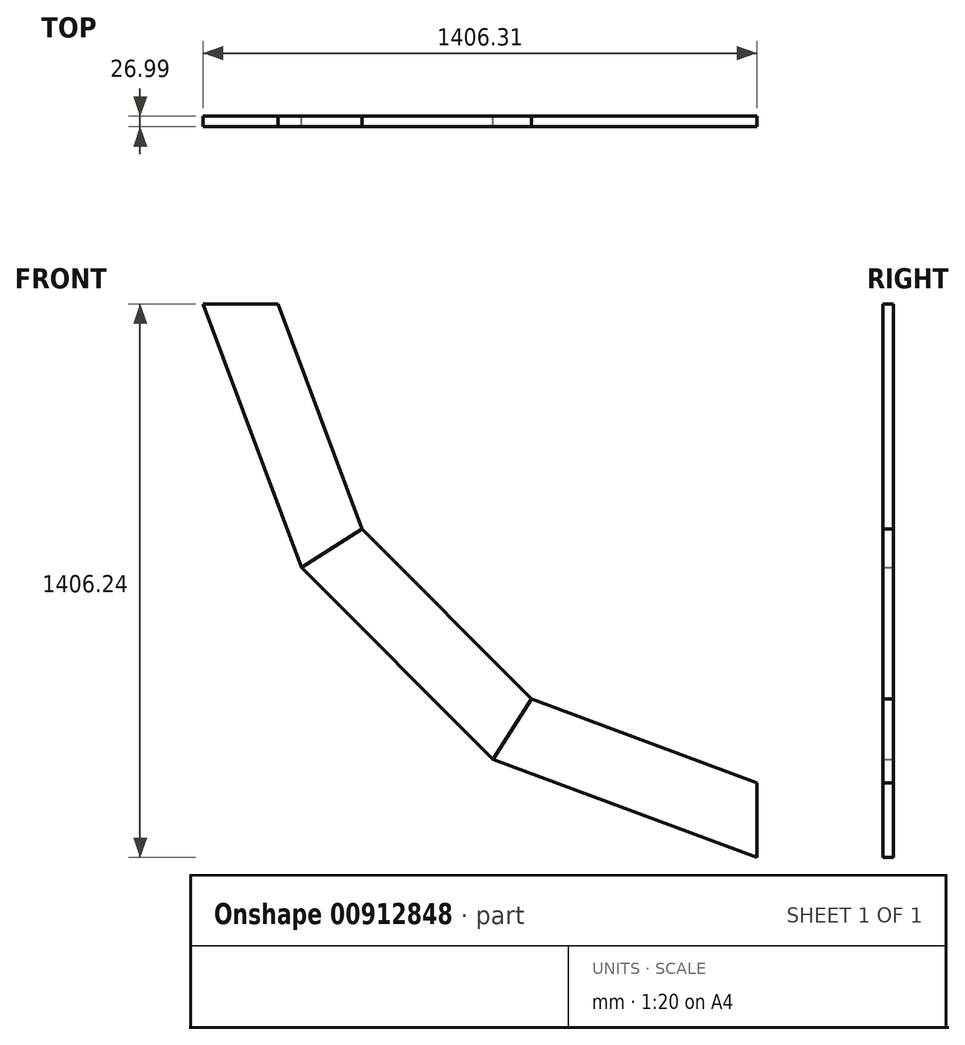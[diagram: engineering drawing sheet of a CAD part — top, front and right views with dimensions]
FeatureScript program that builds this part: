
annotation { "Feature Type Name" : "Feature", "Feature Type Description" : "" }
export const myFeature = defineFeature(function(context is Context, id is Id, definition is map)
    precondition{}
    {
        {
            var Q0;
            Q0=qCreatedBy(makeId("Front.planeOp"),FACE);
            var sketch = newSketch(context, id + "F0", { "sketchPlane" : qUnion([Q0])});
            skLineSegment(sketch, "E0", {"start": v(2153.22, 0) * mm, "end": v(0, 0) * mm, "construction": true});
            skLineSegment(sketch, "E1", {"start": v(0, 0) * mm, "end": v(0, 1924.25) * mm, "construction": true});
            skArc(sketch, "E2", {"start": v(0, 1275.2) * mm, "mid": v(409.72, 409.72) * mm, "end": v(1275.2, 0) * mm});
            skLineSegment(sketch, "E3", {"start": v(0, 1275.2) * mm, "end": v(1275.2, 0) * mm, "construction": true});
            skArc(sketch, "E4.0", {"start": v(51.06, 1275.2) * mm, "mid": v(445.65, 445.65) * mm, "end": v(1275.2, 51.06) * mm});
            skArc(sketch, "E5.0", {"start": v(-63.8, 1275.2) * mm, "mid": v(364.82, 364.82) * mm, "end": v(1275.2, -63.8) * mm});
            skLineSegment(sketch, "E6", {"start": v(-728.5, 1275.2) * mm, "end": v(574.74, 1275.2) * mm, "construction": true});
            skLineSegment(sketch, "E7", {"start": v(1275.2, -744.23) * mm, "end": v(1275.2, 559) * mm, "construction": true});
            skLineSegment(sketch, "E8", {"start": v(51.06, 1275.2) * mm, "end": v(51.06, 1921.78) * mm});
            skLineSegment(sketch, "E9", {"start": v(-63.8, 1275.2) * mm, "end": v(-63.8, 1924.25) * mm});
            skLineSegment(sketch, "E10", {"start": v(1275.2, 51.06) * mm, "end": v(1997.7, 51.06) * mm});
            skLineSegment(sketch, "E11", {"start": v(1275.2, -63.8) * mm, "end": v(2006.98, -63.8) * mm});
            skLineSegment(sketch, "E12", {"start": v(-728.5, 1275.2) * mm, "end": v(1275.2, -744.23) * mm, "construction": true});
            skLineSegment(sketch, "E13", {"start": v(-131.11, 1275.2) * mm, "end": v(119.08, 605.18) * mm});
            skLineSegment(sketch, "E14", {"start": v(58.68, 1275.2) * mm, "end": v(272.16, 703.49) * mm});
            skLineSegment(sketch, "E15", {"start": v(1275.2, 58.68) * mm, "end": v(703.26, 271.54) * mm});
            skLineSegment(sketch, "E16", {"start": v(1275.2, -131.04) * mm, "end": v(604.84, 118.45) * mm});
            skLineSegment(sketch, "E17", {"start": v(272.16, 703.49) * mm, "end": v(703.26, 271.54) * mm});
            skLineSegment(sketch, "E18", {"start": v(119.08, 605.18) * mm, "end": v(604.84, 118.45) * mm});
            skPoint(sketch, "E19", {"position": v(1275.2, -92.61) * mm});
            skLineSegment(sketch, "E20", {"start": v(703.26, 271.54) * mm, "end": v(604.84, 118.45) * mm});
            skLineSegment(sketch, "E21", {"start": v(1275.2, 58.68) * mm, "end": v(1275.2, -131.04) * mm});
            skLineSegment(sketch, "E22", {"start": v(272.16, 703.49) * mm, "end": v(119.08, 605.18) * mm});
            skLineSegment(sketch, "E23", {"start": v(58.68, 1275.2) * mm, "end": v(-131.11, 1275.2) * mm});
            skPoint(sketch, "E24", {"position": v(-76.88, 1275.2) * mm});
            skLineSegment(sketch, "E25", {"start": v(-36.22, 1275.2) * mm, "end": v(195.62, 654.33) * mm, "construction": true});
            skLineSegment(sketch, "E26", {"start": v(195.62, 654.33) * mm, "end": v(654.05, 195) * mm, "construction": true});
            skLineSegment(sketch, "E27", {"start": v(654.05, 195) * mm, "end": v(1275.2, -36.18) * mm, "construction": true});
            skSolve(sketch);
        }
        {
            var Q0;
            {var subQ5=sQuery(id+"F0.wireOp",EDGE,"E14");Q0=makeQuery(id+"F0.imprint","IMPRINT",FACE,{"disambiguationData":[TD([[makeQuery(id+"F0.imprint","IMPRINT",EDGE,{"derivedFrom":subQ5}),-1.0]])]});}
            var Q1;
            {var subQ0=sQuery(id+"F0.wireOp",EDGE,"E23");var subQ1=sQuery(id+"F0.wireOp",EDGE,"E2");var subQ2=makeQuery(id+"F0.imprint","INTERSECT",VERTEX,{"derivedFrom":[subQ1,subQ0]});Q1=makeQuery(id+"F0.imprint","IMPRINT",FACE,{"disambiguationData":[TD([[makeQuery(id+"F0.imprint","IMPRINT",EDGE,{"disambiguationData":[TD([[subQ2,-1.0]])],"derivedFrom":subQ1}),1.0]])]});}
            var Q2;
            {var subQ0=sQuery(id+"F0.wireOp",EDGE,"E23");var subQ1=sQuery(id+"F0.wireOp",EDGE,"E2");var subQ2=makeQuery(id+"F0.imprint","INTERSECT",VERTEX,{"derivedFrom":[subQ1,subQ0]});Q2=makeQuery(id+"F0.imprint","IMPRINT",FACE,{"disambiguationData":[TD([[makeQuery(id+"F0.imprint","IMPRINT",EDGE,{"disambiguationData":[TD([[subQ2,-1.0]])],"derivedFrom":subQ1}),-1.0]])]});}
            var Q3;
            {var subQ5=sQuery(id+"F0.wireOp",EDGE,"E13");Q3=makeQuery(id+"F0.imprint","IMPRINT",FACE,{"disambiguationData":[TD([[makeQuery(id+"F0.imprint","IMPRINT",EDGE,{"derivedFrom":subQ5}),1.0]])]});}
            var Q4;
            {var subQ5=sQuery(id+"F0.wireOp",EDGE,"E15");Q4=makeQuery(id+"F0.imprint","IMPRINT",FACE,{"disambiguationData":[TD([[makeQuery(id+"F0.imprint","IMPRINT",EDGE,{"derivedFrom":subQ5}),1.0]])]});}
            var Q5;
            {var subQ0=sQuery(id+"F0.wireOp",EDGE,"E21");var subQ1=sQuery(id+"F0.wireOp",EDGE,"E2");var subQ2=makeQuery(id+"F0.imprint","INTERSECT",VERTEX,{"derivedFrom":[subQ1,subQ0]});Q5=makeQuery(id+"F0.imprint","IMPRINT",FACE,{"disambiguationData":[TD([[makeQuery(id+"F0.imprint","IMPRINT",EDGE,{"disambiguationData":[TD([[subQ2,1.0]])],"derivedFrom":subQ1}),1.0]])]});}
            var Q6;
            {var subQ0=sQuery(id+"F0.wireOp",EDGE,"E21");var subQ1=sQuery(id+"F0.wireOp",EDGE,"E2");var subQ2=makeQuery(id+"F0.imprint","INTERSECT",VERTEX,{"derivedFrom":[subQ1,subQ0]});Q6=makeQuery(id+"F0.imprint","IMPRINT",FACE,{"disambiguationData":[TD([[makeQuery(id+"F0.imprint","IMPRINT",EDGE,{"disambiguationData":[TD([[subQ2,1.0]])],"derivedFrom":subQ1}),-1.0]])]});}
            var Q7;
            {var subQ5=sQuery(id+"F0.wireOp",EDGE,"E16");Q7=makeQuery(id+"F0.imprint","IMPRINT",FACE,{"disambiguationData":[TD([[makeQuery(id+"F0.imprint","IMPRINT",EDGE,{"derivedFrom":subQ5}),-1.0]])]});}
            extrude(context, id + "F1", {"entities" : qUnion([Q0, Q1, Q2, Q3, Q4, Q5, Q6, Q7]), "depth" : 26.99 * mm, "offsetDistance" : 25.4 * mm});
        }
        {
            var Q0;
            {var subQ5=sQuery(id+"F0.wireOp",EDGE,"E17");Q0=makeQuery(id+"F0.imprint","IMPRINT",FACE,{"disambiguationData":[TD([[makeQuery(id+"F0.imprint","IMPRINT",EDGE,{"derivedFrom":subQ5}),-1.0]])]});}
            var Q1;
            {var subQ0=sQuery(id+"F0.wireOp",EDGE,"E22");var subQ1=sQuery(id+"F0.wireOp",EDGE,"E2");var subQ2=makeQuery(id+"F0.imprint","INTERSECT",VERTEX,{"derivedFrom":[subQ1,subQ0]});Q1=makeQuery(id+"F0.imprint","IMPRINT",FACE,{"disambiguationData":[TD([[makeQuery(id+"F0.imprint","IMPRINT",EDGE,{"disambiguationData":[TD([[subQ2,-1.0]])],"derivedFrom":subQ1}),1.0]])]});}
            var Q2;
            {var subQ0=sQuery(id+"F0.wireOp",EDGE,"E22");var subQ1=sQuery(id+"F0.wireOp",EDGE,"E2");var subQ2=makeQuery(id+"F0.imprint","INTERSECT",VERTEX,{"derivedFrom":[subQ1,subQ0]});Q2=makeQuery(id+"F0.imprint","IMPRINT",FACE,{"disambiguationData":[TD([[makeQuery(id+"F0.imprint","IMPRINT",EDGE,{"disambiguationData":[TD([[subQ2,-1.0]])],"derivedFrom":subQ1}),-1.0]])]});}
            var Q3;
            {var subQ5=sQuery(id+"F0.wireOp",EDGE,"E18");Q3=makeQuery(id+"F0.imprint","IMPRINT",FACE,{"disambiguationData":[TD([[makeQuery(id+"F0.imprint","IMPRINT",EDGE,{"derivedFrom":subQ5}),1.0]])]});}
            extrude(context, id + "F2", {"entities" : qUnion([Q0, Q1, Q2, Q3]), "depth" : 26.99 * mm, "offsetDistance" : 25.4 * mm});
        }
    });
